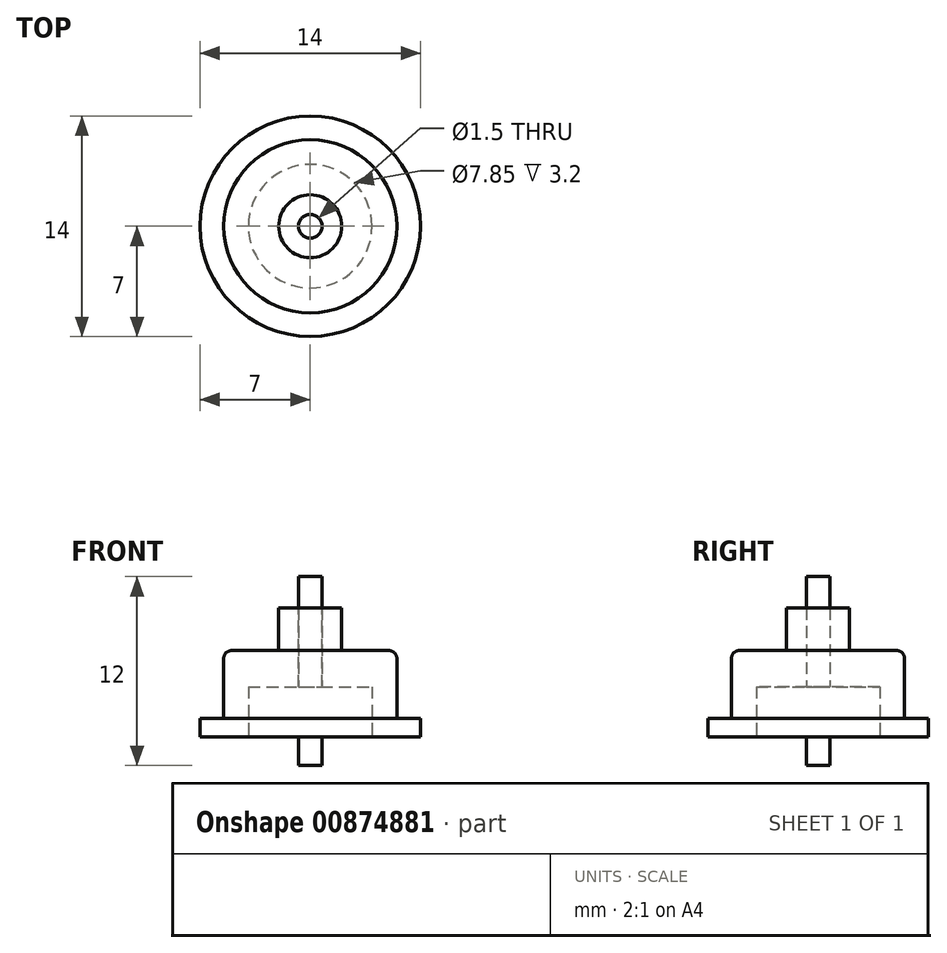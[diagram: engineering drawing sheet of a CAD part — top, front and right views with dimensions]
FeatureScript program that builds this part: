
annotation { "Feature Type Name" : "Feature", "Feature Type Description" : "" }
export const myFeature = defineFeature(function(context is Context, id is Id, definition is map)
    precondition{}
    {
        {
            var Q0;
            Q0=qCreatedBy(makeId("Top.planeOp"),FACE);
            var sketch = newSketch(context, id + "F0", { "sketchPlane" : qUnion([Q0])});
            skCircle(sketch, "E0", {"center": v(0, 0) * mm, "radius": 7 * mm});
            skCircle(sketch, "E1", {"center": v(0, 0) * mm, "radius": 2 * mm});
            skCircle(sketch, "E2", {"center": v(0, 0) * mm, "radius": 0.75 * mm});
            skCircle(sketch, "E3", {"center": v(0, 0) * mm, "radius": 5.5 * mm});
            skSolve(sketch);
        }
        {
            var Q0;
            Q0=makeQuery(id+"F0.imprint","IMPRINT",FACE,{"disambiguationData":[TD([[makeQuery(id+"F0.imprint","IMPRINT",EDGE,{"derivedFrom":sQuery(id+"F0.wireOp",EDGE,"E0")}),1.0]])]});
            var Q1;
            Q1=makeQuery(id+"F0.imprint","IMPRINT",FACE,{"disambiguationData":[TD([[makeQuery(id+"F0.imprint","IMPRINT",EDGE,{"derivedFrom":sQuery(id+"F0.wireOp",EDGE,"E1")}),-1.0]])]});
            var Q2;
            Q2=makeQuery(id+"F0.imprint","IMPRINT",FACE,{"disambiguationData":[TD([[makeQuery(id+"F0.imprint","IMPRINT",EDGE,{"derivedFrom":sQuery(id+"F0.wireOp",EDGE,"E1")}),1.0]])]});
            var Q3;
            Q3=makeQuery(id+"F0.imprint","IMPRINT",FACE,{"disambiguationData":[TD([[makeQuery(id+"F0.imprint","IMPRINT",EDGE,{"derivedFrom":sQuery(id+"F0.wireOp",EDGE,"E3")}),1.0]])]});
            extrude(context, id + "F1", {"entities" : qUnion([Q0, Q1, Q2, Q3]), "oppositeDirection" : true, "depth" : 1.2 * mm, "offsetDistance" : 25 * mm});
        }
        {
            var Q0;
            Q0=makeQuery(id+"F0.imprint","IMPRINT",FACE,{"disambiguationData":[TD([[makeQuery(id+"F0.imprint","IMPRINT",EDGE,{"derivedFrom":sQuery(id+"F0.wireOp",EDGE,"E1")}),1.0]])]});
            extrude(context, id + "F2", {"entities" : qUnion([Q0]), "operationType" : NewBodyOperationType.ADD, "depth" : 7 * mm, "offsetDistance" : 25 * mm});
        }
        {
            var Q0;
            Q0=makeQuery(id+"F0.imprint","IMPRINT",FACE,{"disambiguationData":[TD([[makeQuery(id+"F0.imprint","IMPRINT",EDGE,{"derivedFrom":sQuery(id+"F0.wireOp",EDGE,"E2")}),1.0]])]});
            extrude(context, id + "F3", {"entities" : qUnion([Q0]), "depth" : 9 * mm, "offsetDistance" : 25 * mm, "hasSecondDirection" : true, "secondDirectionOppositeDirection" : true, "secondDirectionDepth" : 3 * mm});
        }
        {
            var Q0;
            Q0=makeQuery(id+"F0.imprint","IMPRINT",FACE,{"disambiguationData":[TD([[makeQuery(id+"F0.imprint","IMPRINT",EDGE,{"derivedFrom":sQuery(id+"F0.wireOp",EDGE,"E1")}),-1.0]])]});
            var Q1;
            Q1=makeQuery(id+"F0.imprint","IMPRINT",FACE,{"disambiguationData":[TD([[makeQuery(id+"F0.imprint","IMPRINT",EDGE,{"derivedFrom":sQuery(id+"F0.wireOp",EDGE,"E3")}),1.0]])]});
            extrude(context, id + "F4", {"entities" : qUnion([Q0, Q1]), "operationType" : NewBodyOperationType.ADD, "depth" : 4.3 * mm, "offsetDistance" : 25 * mm});
        }
        {
            var Q0;
            Q0=makeQuery(id+"F4.opExtrude","CAP_EDGE",EDGE,{"disambiguationData":[OSD([sQuery(id+"F0.wireOp",EDGE,"E3")])],"isStart":false});
            fillet(context, id + "F5", {"entities" : qUnion([Q0]), "radius" : .5 * mm, "tangentPropagation" : true, "allowEdgeOverflow" : false});
        }
        {
            var Q0;
            Q0=makeQuery(id+"F1.opExtrude","CAP_FACE",FACE,{"disambiguationData":[OSD([sQuery(id+"F0.wireOp",EDGE,"E0"),sQuery(id+"F0.wireOp",EDGE,"E2")])],"isStart":false});
            var sketch = newSketch(context, id + "F6", { "sketchPlane" : qUnion([Q0])});
            skCircle(sketch, "E4", {"center": v(0, 0) * mm, "radius": 3.92 * mm});
            skSolve(sketch);
        }
        {
            var Q0;
            Q0 = qSketchRegion(id + "F6", true);
            extrude(context, id + "F7", {"entities" : qUnion([Q0]), "operationType" : NewBodyOperationType.REMOVE, "oppositeDirection" : true, "depth" : 3.2 * mm, "offsetDistance" : 25 * mm});
        }
    });
